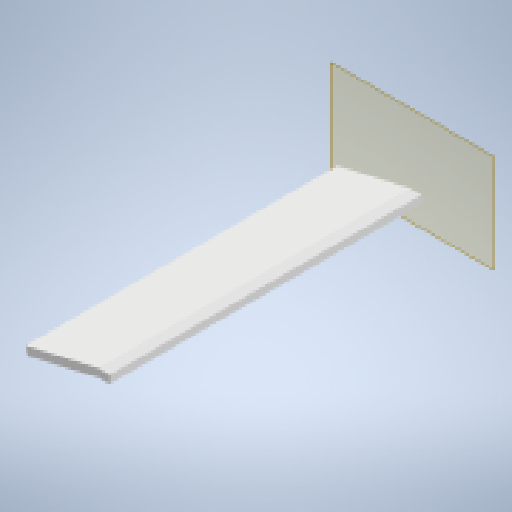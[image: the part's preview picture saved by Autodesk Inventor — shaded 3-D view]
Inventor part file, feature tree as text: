
AUTODESK INVENTOR PART (.ipt)
format: ipt  version: 2023 (Build 270158030, 158C)  size: 147,456 bytes
history: native  units: mm
features: other x4, plane x1, extrude x1, sketch x1, reference x1
ambient origin geometry x8: Origin, YZ Plane, XZ Plane, XY Plane, X Axis, Y Axis, Z Axis, Center Point
bodies: Body1 (feature_tree)
feature tree (8):
  other  "backrest"
  plane  "Work Plane1"
  extrude  "Extrusion1"  [1 undecoded]
  sketch  "Sketch1"  dims[d0=1930.0mm d1=0.0mm]
  reference  "Reference1"
  other  "<userpath>\Documents\0004-inventor\3D-CAD-main\primary-engineer-bench.iam"
  other  "primary-engineer-bench.iam"
  other  "bench-end-peice:1"
note: 1 required parameter value undecoded (feature->parameter linkage not recoverable at this tier; creation-order binding heuristic only, values carry confidence <= 0.55)
